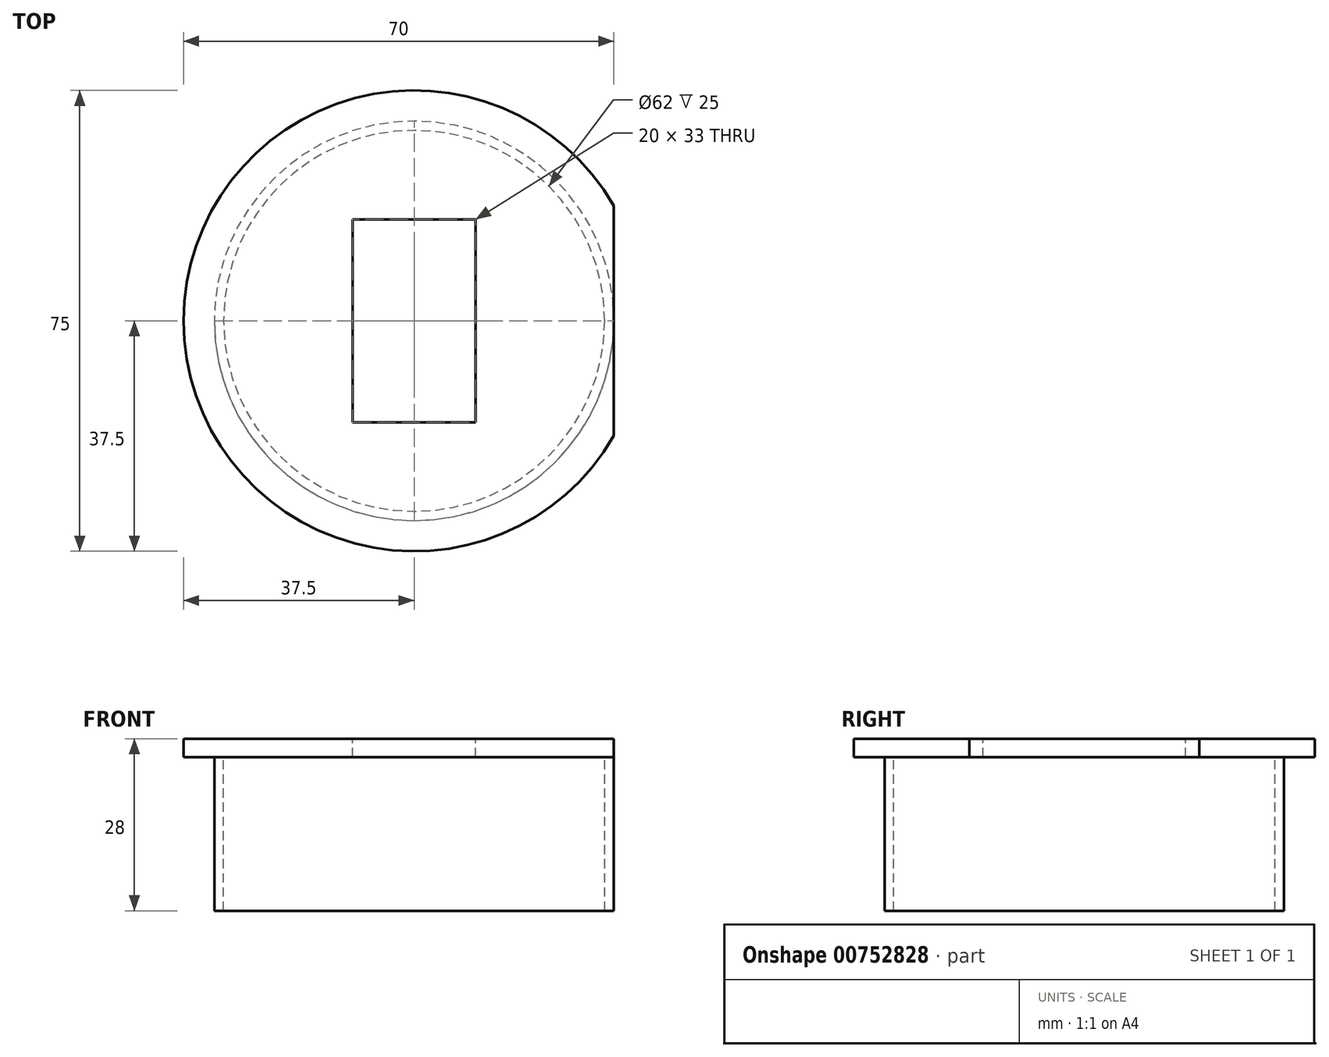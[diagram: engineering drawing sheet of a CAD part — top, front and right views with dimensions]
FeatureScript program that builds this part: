
annotation { "Feature Type Name" : "Feature", "Feature Type Description" : "" }
export const myFeature = defineFeature(function(context is Context, id is Id, definition is map)
    precondition{}
    {
        {
            var Q0;
            Q0=qCreatedBy(makeId("Top.planeOp"),FACE);
            var sketch = newSketch(context, id + "F0", { "sketchPlane" : qUnion([Q0])});
            skCircle(sketch, "E0", {"center": v(0, 0) * mm, "radius": 37.5 * mm});
            skSolve(sketch);
        }
        {
            var Q0;
            Q0 = qSketchRegion(id + "F0", true);
            extrude(context, id + "F1", {"entities" : qUnion([Q0]), "depth" : 3 * mm, "offsetDistance" : 25 * mm});
        }
        {
            var Q0;
            Q0=makeQuery(id+"F1.opExtrude","CAP_FACE",FACE,{"disambiguationData":[OSD([sQuery(id+"F0.wireOp",EDGE,"E0")])],"isStart":true});
            var sketch = newSketch(context, id + "F2", { "sketchPlane" : qUnion([Q0])});
            skCircle(sketch, "E1", {"center": v(0, 0) * mm, "radius": 32.5 * mm});
            skCircle(sketch, "E2", {"center": v(0, 0) * mm, "radius": 31 * mm});
            skSolve(sketch);
        }
        {
            var Q0;
            Q0 = qSketchRegion(id + "F2", true);
            extrude(context, id + "F3", {"entities" : qUnion([Q0]), "operationType" : NewBodyOperationType.ADD, "depth" : 25 * mm, "offsetDistance" : 25 * mm});
        }
        {
            var Q0;
            Q0=makeQuery(id+"F1.opExtrude","CAP_FACE",FACE,{"disambiguationData":[OSD([sQuery(id+"F0.wireOp",EDGE,"E0")])],"isStart":false});
            var sketch = newSketch(context, id + "F4", { "sketchPlane" : qUnion([Q0])});
            skLineSegment(sketch, "E3.bottom", {"start": v(10, 16.5) * mm, "end": v(-10, 16.5) * mm});
            skLineSegment(sketch, "E3.top", {"start": v(10, -16.5) * mm, "end": v(-10, -16.5) * mm});
            skLineSegment(sketch, "E3.left", {"start": v(10, 16.5) * mm, "end": v(10, -16.5) * mm});
            skLineSegment(sketch, "E3.right", {"start": v(-10, 16.5) * mm, "end": v(-10, -16.5) * mm});
            skPoint(sketch, "E3.middle", {"position": v(0, 0) * mm});
            skSolve(sketch);
        }
        {
            var Q0;
            Q0 = qSketchRegion(id + "F4", true);
            extrude(context, id + "F5", {"entities" : qUnion([Q0]), "operationType" : NewBodyOperationType.REMOVE, "oppositeDirection" : true, "depth" : 25 * mm, "offsetDistance" : 25 * mm});
        }
        {
            var Q0;
            {var subQ0=sQuery(id+"F0.wireOp",EDGE,"E0");Q0=makeQuery(id+"F3.boolean.opBoolean","SPLIT",FACE,{"disambiguationData":[TD([makeQuery(id+"F1.opExtrude","SWEPT_FACE",FACE,{"disambiguationData":[OSD([subQ0])]})])],"derivedFrom":makeQuery(id+"F1.opExtrude","CAP_FACE",FACE,{"disambiguationData":[OSD([subQ0])],"isStart":true})});}
            var sketch = newSketch(context, id + "F6", { "sketchPlane" : qUnion([Q0])});
            skLineSegment(sketch, "E4.bottom", {"start": v(32.5, -18.7) * mm, "end": v(40.57, -18.7) * mm});
            skLineSegment(sketch, "E4.top", {"start": v(32.5, 19.71) * mm, "end": v(40.57, 19.71) * mm});
            skLineSegment(sketch, "E4.left", {"start": v(32.5, -18.7) * mm, "end": v(32.5, 19.71) * mm});
            skLineSegment(sketch, "E4.right", {"start": v(40.57, -18.7) * mm, "end": v(40.57, 19.71) * mm});
            skSolve(sketch);
        }
        {
            var Q0;
            Q0 = qSketchRegion(id + "F6", true);
            extrude(context, id + "F7", {"entities" : qUnion([Q0]), "operationType" : NewBodyOperationType.REMOVE, "oppositeDirection" : true, "depth" : 25 * mm, "offsetDistance" : 25 * mm});
        }
    });
